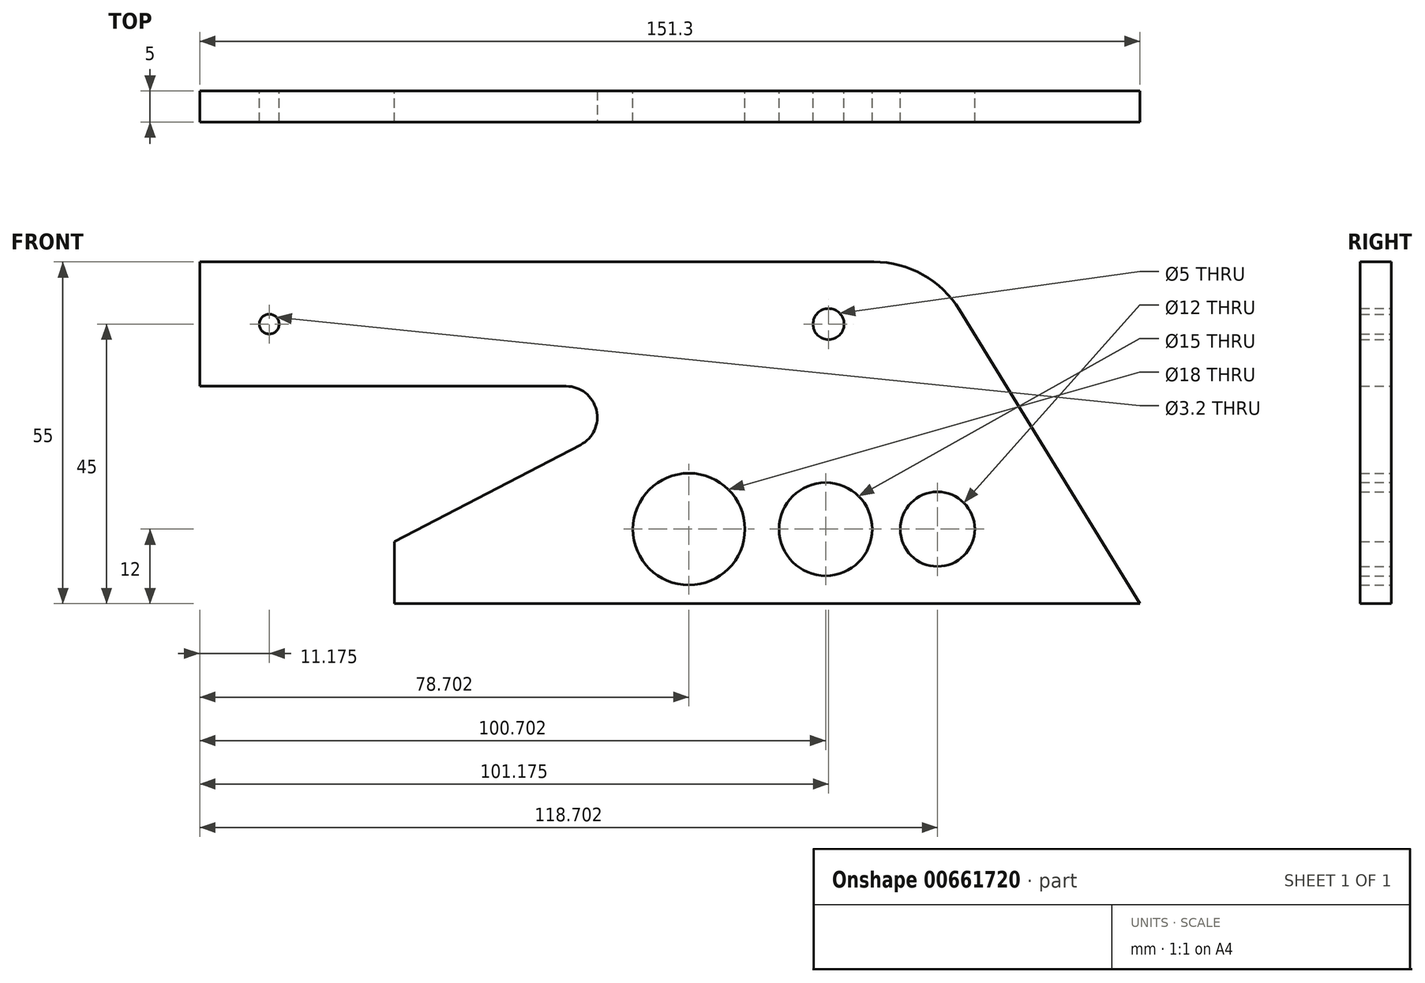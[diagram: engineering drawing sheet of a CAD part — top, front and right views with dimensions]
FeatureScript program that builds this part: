
annotation { "Feature Type Name" : "Feature", "Feature Type Description" : "" }
export const myFeature = defineFeature(function(context is Context, id is Id, definition is map)
    precondition{}
    {
        {
            var Q0;
            Q0=qCreatedBy(makeId("Front.planeOp"),FACE);
            var sketch = newSketch(context, id + "F0", { "sketchPlane" : qUnion([Q0])});
            skLineSegment(sketch, "E0", {"start": v(-0.25, 20) * mm, "end": v(77.15, 20) * mm});
            skArc(sketch, "E1", {"start": v(77.15, 20) * mm, "mid": v(85.06, 17.94) * mm, "end": v(90.96, 12.27) * mm});
            skLineSegment(sketch, "E2", {"start": v(90.96, 12.27) * mm, "end": v(120, -35) * mm});
            skLineSegment(sketch, "E3", {"start": v(120, -35) * mm, "end": v(0, -35) * mm});
            skLineSegment(sketch, "E4", {"start": v(0, -35) * mm, "end": v(0, -25) * mm});
            skLineSegment(sketch, "E5", {"start": v(0, -25) * mm, "end": v(31.68, -8.54) * mm});
            skArc(sketch, "E6", {"start": v(31.68, -8.54) * mm, "mid": v(34.71, -4.78) * mm, "end": v(33.98, 0) * mm});
            skLineSegment(sketch, "E7", {"start": v(33.98, 0) * mm, "end": v(0, 0) * mm});
            skCircle(sketch, "E8", {"center": v(47.4, -23) * mm, "radius": 9 * mm});
            skCircle(sketch, "E9", {"center": v(69.4, -23) * mm, "radius": 7.5 * mm});
            skCircle(sketch, "E10", {"center": v(87.4, -23) * mm, "radius": 6 * mm});
            skCircle(sketch, "E11", {"center": v(69.87, 10) * mm, "radius": 2.5 * mm});
            skCircle(sketch, "E12", {"center": v(-20.13, 10) * mm, "radius": 1.6 * mm});
            skLineSegment(sketch, "E13.bottom", {"start": v(-0.25, 20) * mm, "end": v(-29.06, 20) * mm});
            skLineSegment(sketch, "E13.top", {"start": v(0, 0) * mm, "end": v(-31.3, 0) * mm});
            skLineSegment(sketch, "E14", {"start": v(-31.3, 0) * mm, "end": v(-31.3, 20) * mm});
            skLineSegment(sketch, "E15", {"start": v(-31.3, 20) * mm, "end": v(-29.06, 20) * mm});
            skSolve(sketch);
        }
        {
            var Q0;
            Q0 = qSketchRegion(id + "F0", true);
            extrude(context, id + "F1", {"entities" : qUnion([Q0]), "depth" : 5 * mm, "offsetDistance" : 25 * mm});
        }
        {
            var Q0;
            Q0=makeQuery(id+"F1.opExtrude","SWEPT_EDGE",EDGE,{"disambiguationData":[OSD([sQuery(id+"F0.wireOp",EDGE,"zll1Kxso-SlGK-Gg0s-I3T3-TKECvArxRueF"),sQuery(id+"F0.wireOp",EDGE,"E0")])]});
            var Q1;
            Q1=makeQuery(id+"F1.opExtrude","SWEPT_EDGE",EDGE,{"disambiguationData":[OSD([sQuery(id+"F0.wireOp",EDGE,"zll1Kxso-SlGK-Gg0s-I3T3-TKECvArxRueF"),sQuery(id+"F0.wireOp",EDGE,"E7")])]});
            fillet(context, id + "F2", {"entities" : qUnion([Q0, Q1]), "radius" : 5 * mm, "tangentPropagation" : true, "allowEdgeOverflow" : false});
        }
    });
